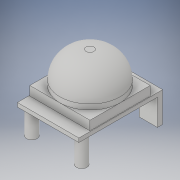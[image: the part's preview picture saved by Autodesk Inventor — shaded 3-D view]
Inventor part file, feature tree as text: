
AUTODESK INVENTOR PART (.ipt)
format: ipt  version: 2017.2 (Build 212223000, 223)  size: 180,224 bytes
history: native  units: in
note: dims shown in document units (in); Inventor stores cm internally (conversion verified against a paired STEP export)
features: extrude x6, sketch x6, fillet x1
ambient origin geometry x8: Origin, YZ Plane, XZ Plane, XY Plane, X Axis, Y Axis, Z Axis, Center Point
bodies: Solid1 (feature_tree)
feature tree (13):
  extrude  "Extrusion1"  Depth=1.2598in
  extrude  "Extrusion2"  Depth=0.9055in
  extrude  "Extrusion3"  Depth=0.1378in TaperAngle=0.0deg
  fillet  "Fillet1"  Radius=0.9055in
  sketch  "Sketch4"  dims[d9=0.4724in d10=0.0in d11=0.3937in]
  extrude  "Extrusion4"  Depth=0.3937in
  extrude  "Extrusion5"  Depth=0.1575in
  extrude  "Extrusion6"  Depth=0.0787in
  sketch  "Sketch1"  dims[d0=0.9252in d1=1.2598in]
  sketch  "Sketch2"  dims[d2=0.0591in d3=0.0in d4=0.9055in]
  sketch  "Sketch3"  dims[d5=0.9055in d6=0.1378in d7=0.0in d8=0.9055in]
  sketch  "Sketch5"  dims[d13=0.1575in d14=0.1575in]
  sketch  "Sketch6"  dims[d16=0.2756in d17=0.0787in d18=0.3937in d19=0.0in d20=0.1575in d21=0.2756in d22=0.0787in d23=0.3937in d24=0.0in d26=0.1575in d27=0.1575in d28=0.1575in d29=0.3937in d30=0.0in]
